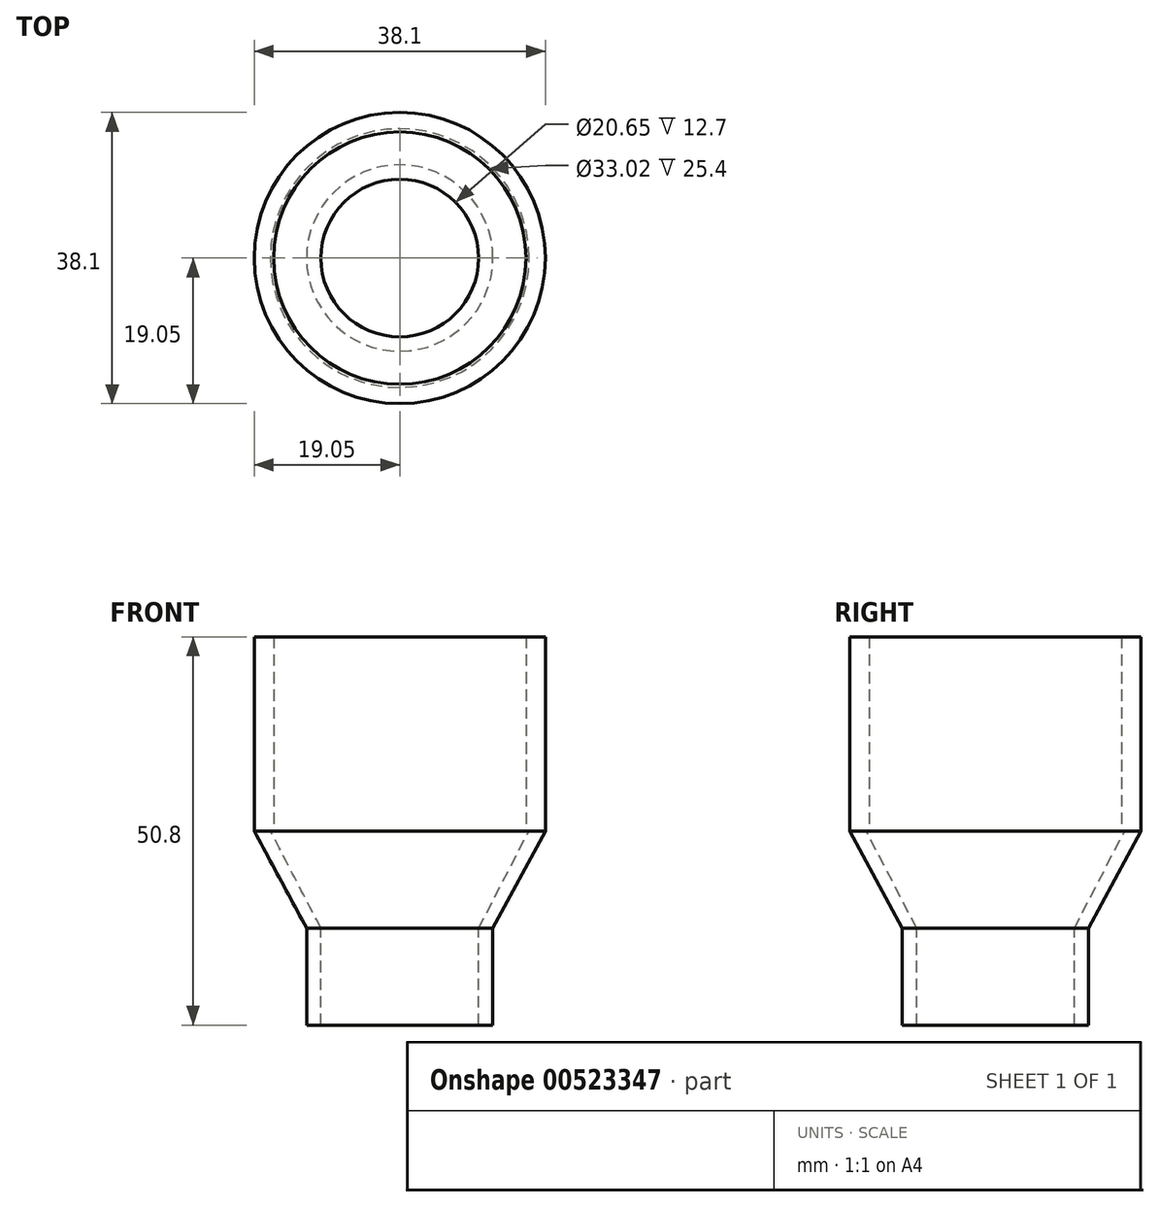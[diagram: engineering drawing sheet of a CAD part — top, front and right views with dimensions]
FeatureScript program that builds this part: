
annotation { "Feature Type Name" : "Feature", "Feature Type Description" : "" }
export const myFeature = defineFeature(function(context is Context, id is Id, definition is map)
    precondition{}
    {
        {
            var Q0;
            Q0=qCreatedBy(makeId("Top.planeOp"),FACE);
            var sketch = newSketch(context, id + "F0", { "sketchPlane" : qUnion([Q0])});
            skPoint(sketch, "E0.middle", {"position": v(0, 0) * mm});
            skCircle(sketch, "E1", {"center": v(0, 0) * mm, "radius": 19.05 * mm});
            skCircle(sketch, "E2", {"center": v(0, 0) * mm, "radius": 16.51 * mm});
            skSolve(sketch);
        }
        {
            var Q0;
            Q0=qSketchRegion(id+"F0",true);
            extrude(context, id + "F1", {"entities" : qUnion([Q0]), "depth" : 25.4 * mm, "offsetDistance" : 25.4 * mm});
        }
        {
            var Q0;
            Q0=qCreatedBy(makeId("Top.planeOp"),FACE);
            cPlane(context, id + "F2", {"entities" : qUnion([Q0]), "cplaneType" : CPlaneType.OFFSET, "offset" : 12.7 * mm, "oppositeDirection" : true, "width" : 152.4 * mm, "height" : 152.4 * mm});
        }
        {
            var Q0;
            Q0=qCreatedBy(id+"F2.planeOp",FACE);
            var sketch = newSketch(context, id + "F3", { "sketchPlane" : qUnion([Q0])});
            skCircle(sketch, "E3", {"center": v(0, 0) * mm, "radius": 12.2 * mm});
            skCircle(sketch, "E4", {"center": v(0, 0) * mm, "radius": 10.33 * mm});
            skSolve(sketch);
        }
        {
            var Q0;
            Q0=qSketchRegion(id+"F3",true);
            extrude(context, id + "F4", {"entities" : qUnion([Q0]), "oppositeDirection" : true, "depth" : 12.7 * mm, "offsetDistance" : 25.4 * mm});
        }
        {
            var Q0;
            Q0=qCreatedBy(makeId("Front.planeOp"),FACE);
            var sketch = newSketch(context, id + "F5", { "sketchPlane" : qUnion([Q0])});
            skLineSegment(sketch, "E5", {"start": v(-19.05, 0) * mm, "end": v(-12.2, -12.72) * mm});
            skLineSegment(sketch, "E6", {"start": v(-12.2, -12.72) * mm, "end": v(-10.31, -12.72) * mm});
            skLineSegment(sketch, "E7", {"start": v(-10.31, -12.72) * mm, "end": v(-16.93, 0) * mm});
            skLineSegment(sketch, "E8", {"start": v(-16.93, 0) * mm, "end": v(-19.05, 0) * mm});
            skLineSegment(sketch, "E9", {"start": v(0, -15.66) * mm, "end": v(0, 1.42) * mm, "construction": true});
            skSolve(sketch);
        }
        {
            var Q0;
            Q0=makeQuery(id+"F5.imprint","IMPRINT",FACE,{"disambiguationData":[TD([[makeQuery(id+"F5.imprint","IMPRINT",EDGE,{"derivedFrom":sQuery(id+"F5.wireOp",EDGE,"E5")}),1.0]])]});
            var Q1;
            Q1=sQuery(id+"F5.wireOp",EDGE,"E9");
            revolve(context, id + "F6", {"entities" : qUnion([Q0]), "axis" : qUnion([Q1]), "revolveType" : RevolveType.FULL});
        }
    });
